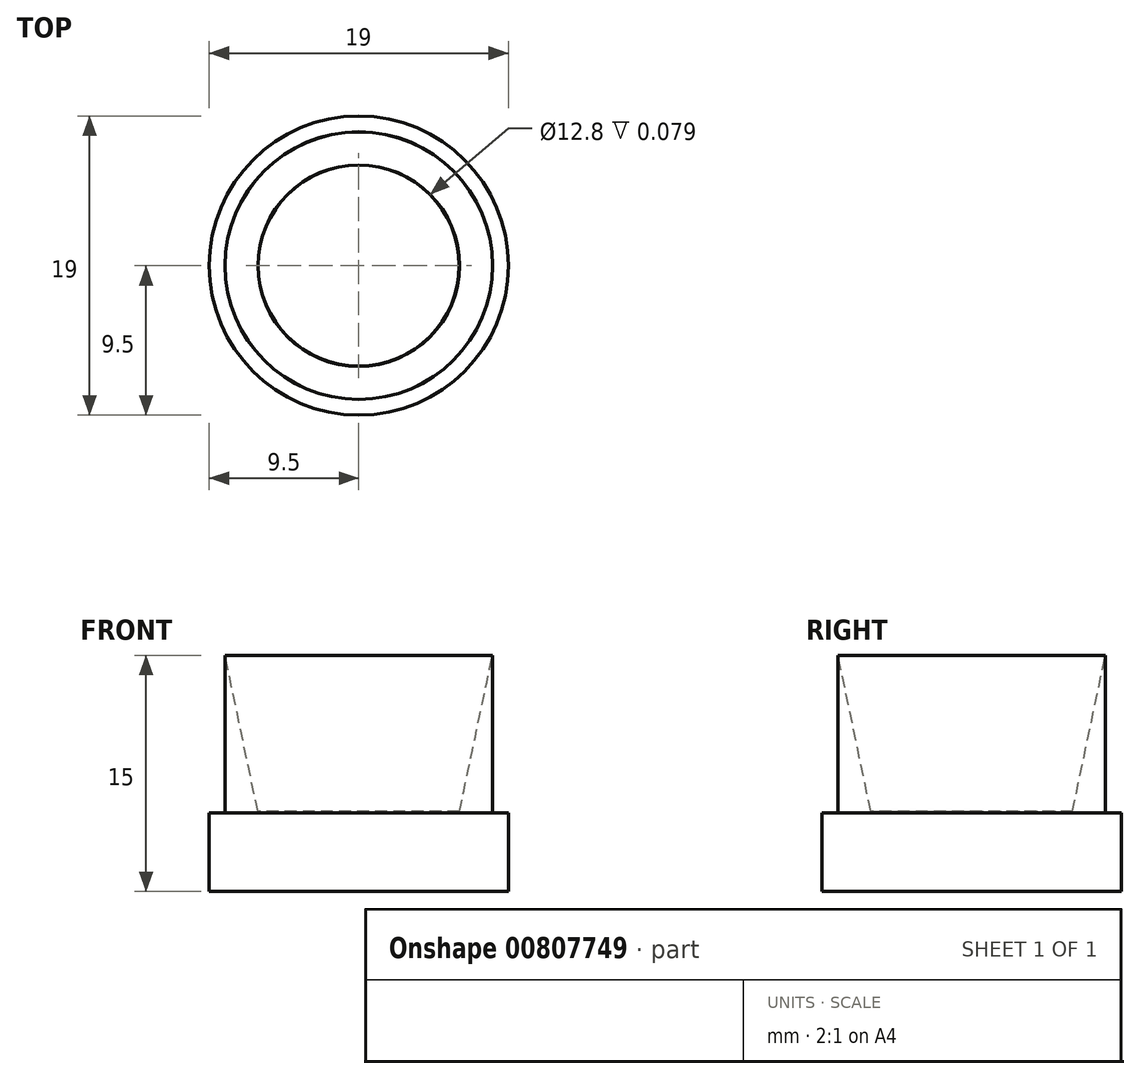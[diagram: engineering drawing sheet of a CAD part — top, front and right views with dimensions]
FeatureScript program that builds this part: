
annotation { "Feature Type Name" : "Feature", "Feature Type Description" : "" }
export const myFeature = defineFeature(function(context is Context, id is Id, definition is map)
    precondition{}
    {
        {
            var Q0;
            Q0=qCreatedBy(makeId("Top.planeOp"),FACE);
            var sketch = newSketch(context, id + "F0", { "sketchPlane" : qUnion([Q0])});
            skCircle(sketch, "E0", {"center": v(0, 0) * mm, "radius": 9.5 * mm});
            skSolve(sketch);
        }
        {
            var Q0;
            Q0=makeQuery(id+"F0.imprint","IMPRINT",FACE,{"disambiguationData":[TD([[makeQuery(id+"F0.imprint","IMPRINT",EDGE,{"derivedFrom":sQuery(id+"F0.wireOp",EDGE,"E0")}),1.0]])]});
            extrude(context, id + "F1", {"entities" : qUnion([Q0]), "depth" : 5 * mm, "offsetDistance" : 25 * mm});
        }
        {
            var Q0;
            Q0=makeQuery(id+"F1.opExtrude","CAP_FACE",FACE,{"disambiguationData":[OSD([sQuery(id+"F0.wireOp",EDGE,"E0")])],"isStart":false});
            var sketch = newSketch(context, id + "F2", { "sketchPlane" : qUnion([Q0])});
            skCircle(sketch, "E1", {"center": v(0, 0) * mm, "radius": 8.5 * mm});
            skCircle(sketch, "E2", {"center": v(0, 0) * mm, "radius": 6.4 * mm});
            skSolve(sketch);
        }
        {
            var Q0;
            Q0=makeQuery(id+"F2.imprint","IMPRINT",FACE,{"disambiguationData":[TD([[makeQuery(id+"F2.imprint","IMPRINT",EDGE,{"derivedFrom":sQuery(id+"F2.wireOp",EDGE,"E1")}),1.0]])]});
            extrude(context, id + "F3", {"entities" : qUnion([Q0]), "operationType" : NewBodyOperationType.ADD, "depth" : 10 * mm, "offsetDistance" : 25 * mm});
        }
        {
            var Q0;
            Q0=qCreatedBy(makeId("Front.planeOp"),FACE);
            var sketch = newSketch(context, id + "F4", { "sketchPlane" : qUnion([Q0])});
            skLineSegment(sketch, "E3", {"start": v(-8.5, 15) * mm, "end": v(-6.4, 15) * mm});
            skLineSegment(sketch, "E4", {"start": v(-6.4, 15) * mm, "end": v(-6.38, 5) * mm});
            skLineSegment(sketch, "E5", {"start": v(-6.38, 5) * mm, "end": v(-8.5, 15) * mm});
            skLineSegment(sketch, "E6", {"start": v(0, 0) * mm, "end": v(0, 15.25) * mm});
            skSolve(sketch);
        }
        {
            var Q0;
            Q0 = qSketchRegion(id + "F4", true);
            var Q1;
            Q1=sQuery(id+"F4.wireOp",EDGE,"E6");
            revolve(context, id + "F5", {"operationType" : NewBodyOperationType.REMOVE, "surfaceOperationType" : NewSurfaceOperationType.NEW, "entities" : qUnion([Q0]), "axis" : qUnion([Q1]), "revolveType" : RevolveType.FULL, "oppositeDirection" : true});
        }
    });
